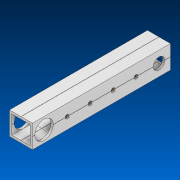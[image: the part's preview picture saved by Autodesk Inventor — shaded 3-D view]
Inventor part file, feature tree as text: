
AUTODESK INVENTOR PART (.ipt)
format: ipt  version: 2022.2 (Build 262287000, 287)  size: 708,608 bytes
history: native  units: in
note: dims shown in document units (in); Inventor stores cm internally (conversion verified against a paired STEP export)
features: other x6, extrude x2, sketch x2, pattern_linear x1, pattern_circular x1
ambient origin geometry x8: Origin, YZ Plane, XZ Plane, XY Plane, X Axis, Y Axis, Z Axis, Center Point
bodies: Solid1 (feature_tree)
feature tree (12):
  extrude  "Extrusion1"  Depth=1.0in
  other  "Work Axis1"
  pattern_linear  "Rectangular Pattern1"  Count1=6  [1 undecoded]
  extrude  "Extrusion2"  Depth=1.0in
  sketch  "Sketch1"  dims[d0=1.0in d1=53.0in]
  other  "Work Axis2"
  other  "Work Axis3"
  other  "Work Axis4"
  other  "Work Axis5"
  other  "Work Axis6"
  sketch  "Sketch2"  dims[d2=0.0in d3=2.3622in d5=1.0in d7=0.0in d8=0.0in d9=0.8in d10=0.25in d11=0.5in]
  pattern_circular  "CirPattern2"
note: 1 required parameter value undecoded (feature->parameter linkage not recoverable at this tier; creation-order binding heuristic only, values carry confidence <= 0.55)
